# Revit family: Oak
name_source: partatom
category: Мебель
revit_build: Autodesk Revit 2017 (Build: 20160225_1515(x64)
units: mm (PartAtom-declared; Revit-internal decimal feet)

## family parameters
Всегда вертикально = Да
Заголовок OmniClass = General Furniture and Specialties
На основе рабочей плоскости = Нет
Номер OmniClass = 23.40.20.00
Общий = Нет
При загрузке вырезать с полостями = Нет
Точка расчета площади = Нет

## types (4) — shared parameters
Dyna = Skandiform Tyg 1
Stol = Skandiform Trä Ek
Изготовитель = Skandiform AB
Ключевая пометка = XBF.2
Комментарии к типоразмеру = Created by Astacus AB
Описание = Stol i ask eller ek med oklädd alt. klädd sits.
Pall i ask eller ek, oklädd sits.
Chair in ash or oak with wooden or upholstered seat.
Stool in ash or oak with wooden seat.

## per-type parameters (varying)
| type | Sits | Typ | URL |
| S-050 | Нет | Oak-stol | http://www.biminfo.se |
| S-049 | Да | Oak-stol | http://www.biminfo.se |
| S-051 | Нет | Oak-pall | http://www.biminfo.se |
| S-052 | Да | Oak-pall | http://file-system.ru |

note: column(s) folded — value = type name in every type: Группа модели

## geometry (parser evidence)
native form markers: Blend x27, Sweep x7
no freeform markers — native parametric forms only
